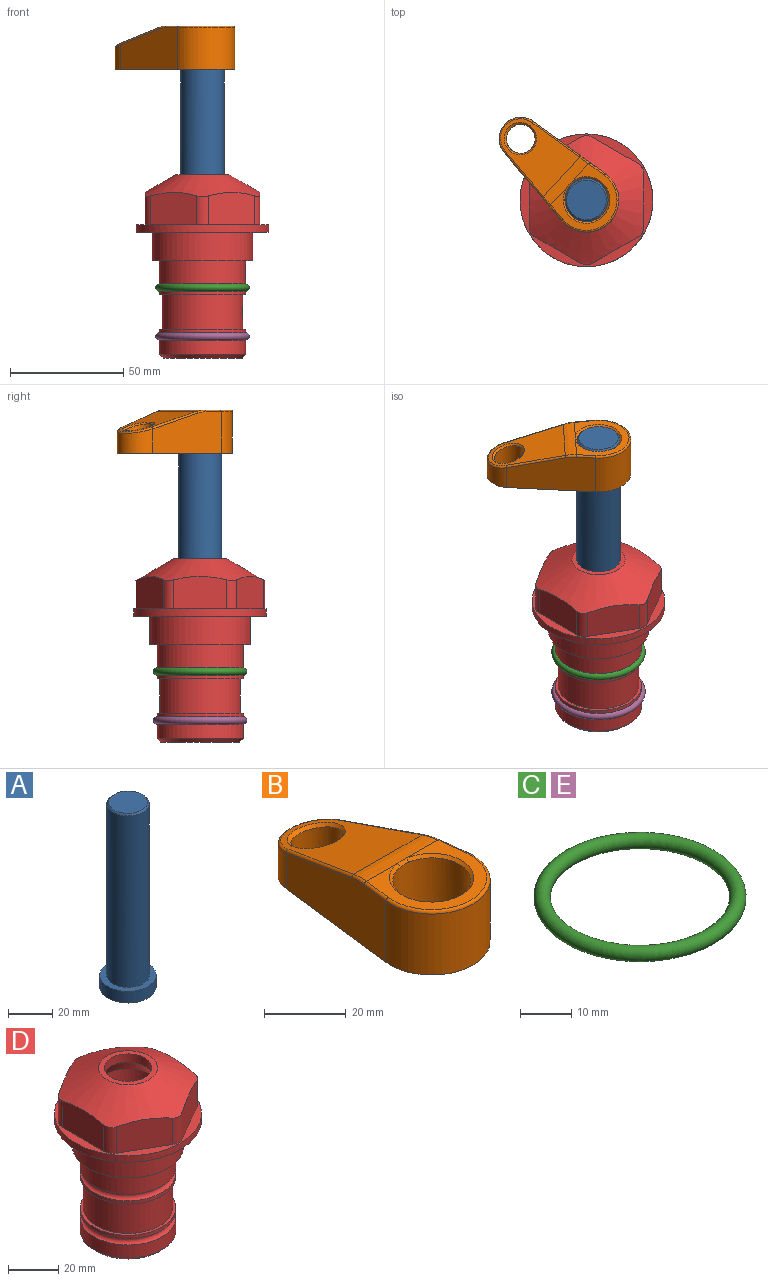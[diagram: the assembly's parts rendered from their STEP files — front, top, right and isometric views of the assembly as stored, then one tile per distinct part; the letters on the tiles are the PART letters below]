
ASSEMBLY  parts=5 mates=4
PART A: 6 faces, bbox 25.4x25.4x101.6 mm
  f0: plane 17.46x17.46mm, normal (0,0,1), area 239.5mm2, adj f5
  f1: plane 25.4x25.4mm, normal (0,0,-1), area 506.7mm2, adj f2
  f2: cylinder r=12.7mm len=25.4mm, axis (0,0,1), area 506.7mm2, adj f1,f3
  f3: plane 25.4x25.4mm, normal (0,0,1), area 221.7mm2, adj f2,f4
  f4: cylinder r=9.53mm len=94.46mm, axis (0,0,1), area 5653mm2, adj f3,f5
  f5: cone r=8.73mm half-angle=45deg, axis (0,0,-1), area 64.4mm2, adj f0,f4
PART B: 31 faces, bbox 31.7x65.5x19.8 mm
  f0: plane 39.12x18.26mm, normal (0.99,0.12,0), area 612.2mm2, adj f1,f4,f7,f11,f13,f15
  f1: cylinder r=9.53mm len=18.91mm, axis (0,0,-1), area 296.1mm2, adj f0,f2,f7,f17
  f2: plane 39.12x18.26mm, normal (-0.99,0.12,0), area 612.2mm2, adj f1,f4,f7,f12,f14,f16
  f3: cylinder r=6.35mm len=12.7mm, axis (0,0,-1), area 362.4mm2, adj f7,f18
  f4: cylinder r=14.29mm len=28.58mm, axis (0,0,-1), area 882.2mm2, adj f0,f2,f7,f10
  f5: cylinder r=9.53mm len=19.05mm, axis (0,0,-1), area 1092.6mm2, adj f7,f19,f20
  f6: plane 26.99x23.69mm, normal (0,0,1), area 216.2mm2, adj f9,f10,f11,f12,f19
  f7: plane 63.5x28.58mm, normal (0,0,-1), area 661.8mm2, adj f0,f1,f2,f3,f4,f5,f22,f23
  f8: plane 33.52x23.6mm, normal (0,0.26,0.97), area 486mm2, adj f9,f15,f16,f17,f18
  f9: cylinder r=19.05mm len=24.72mm, axis (1,0,0), area 120.4mm2, adj f6,f8,f13,f14,f20
  f10: torus R=13.49mm, axis (0,0,1), area 59mm2, adj f4,f6,f11,f12
  f11: cylinder r=0.79mm len=8.67mm, axis (0.12,-0.99,0), area 10.8mm2, adj f0,f6,f10,f13
  f12: cylinder r=0.79mm len=8.67mm, axis (0.12,0.99,0), area 10.8mm2, adj f2,f6,f10,f14
  f13: bspline ~4.95x1.42mm, area 6.1mm2, adj f0,f9,f11,f15
  f14: bspline ~4.95x1.42mm, area 6.1mm2, adj f2,f9,f12,f16
  f15: cylinder r=0.79mm len=25.95mm, axis (0.12,-0.96,0.26), area 32.9mm2, adj f0,f8,f13,f17
  f16: cylinder r=0.79mm len=25.95mm, axis (0.12,0.96,-0.26), area 32.9mm2, adj f2,f8,f14,f17
  f17: bspline ~18.91x8.38mm, area 30mm2, adj f1,f8,f15,f16
  f18: bspline ~14.29x14.29mm, area 48.3mm2, adj f3,f8
  f19: cone r=9.53mm half-angle=45deg, axis (0,0,1), area 66.5mm2, adj f5,f6,f20
  f20: bspline ~3.22x0.96mm, area 3.5mm2, adj f5,f9,f19
  f21: plane 2.75x2.72mm, normal (0,0,-1), area 2.9mm2, adj f23,f25,f28
  f22: plane 23.05x15.88mm, normal (-0.99,-0.12,0), area 323.6mm2, adj f7,f25,f26,f27,f28,f29
  f23: plane 23.05x15.88mm, normal (0.99,-0.12,0), area 323.6mm2, adj f7,f21,f25,f27,f28,f30
  f24: cylinder r=9.53mm len=10.69mm, axis (0,0,-1), area 114.7mm2, adj f7,f27,f29,f30
  f25: cylinder r=12.7mm len=20.59mm, axis (0,0,-1), area 381.1mm2, adj f7,f21,f22,f23,f26,f28
  f26: plane 2.75x2.72mm, normal (0,0,-1), area 2.9mm2, adj f22,f25,f28
  f27: plane 19.72x18.37mm, normal (0,-0.26,-0.97), area 291.8mm2, adj f22,f23,f24,f28,f29,f30
  f28: cylinder r=15.88mm len=19.92mm, axis (1,0,0), area 54.8mm2, adj f21,f22,f23,f25,f26,f27
  f29: cylinder r=1.59mm len=11mm, axis (0,0,-1), area 34.7mm2, adj f7,f22,f24,f27
  f30: cylinder r=1.59mm len=11mm, axis (0,0,-1), area 34.7mm2, adj f7,f23,f24,f27
PART C: 1 faces, bbox 44.7x44.7x3.2 mm
  f0: torus R=19.05mm, axis (0,0,1), area 1193.9mm2
PART D: 36 faces, bbox 58.7x58.7x81 mm
  f0: cylinder r=17.78mm len=35.56mm, axis (0,0,1), area 1670.8mm2, adj f23,f24,f31
  f1: cylinder r=19.05mm len=38.1mm, axis (0,0,1), area 1191.9mm2, adj f26,f27,f30
  f2: plane 58.66x58.66mm, normal (0,0,-1), area 1150.6mm2, adj f3,f28
  f3: cylinder r=29.33mm len=58.66mm, axis (0,0,-1), area 585.1mm2, adj f2,f4
  f4: plane 58.66x58.66mm, normal (0,0,1), area 475.9mm2, adj f3,f5,f6,f7,f8,f9,f10,f11
  f5: plane 20.32x14.34mm, normal (-0.5,0.87,0), area 324.4mm2, adj f4,f15,f16,f17
  f6: plane 20.32x14.34mm, normal (0.5,0.87,0), area 324.4mm2, adj f4,f14,f15,f17
  f7: plane 23.48x14.34mm, normal (1,0,0), area 324.4mm2, adj f4,f13,f14,f17
  f8: plane 20.32x14.34mm, normal (0.5,-0.87,0), area 324.4mm2, adj f4,f12,f13,f17
  f9: plane 20.32x14.34mm, normal (-0.5,-0.87,0), area 324.4mm2, adj f4,f11,f12,f17
  f10: plane 23.48x14.34mm, normal (-1,0,0), area 324.4mm2, adj f4,f11,f16,f17
  f11: cylinder r=5.08mm len=12.85mm, axis (0,0,-1), area 67.2mm2, adj f4,f9,f10,f17
  f12: cylinder r=5.08mm len=12.85mm, axis (0,0,-1), area 67.2mm2, adj f4,f8,f9,f17
  f13: cylinder r=5.08mm len=12.85mm, axis (0,0,-1), area 67.2mm2, adj f4,f7,f8,f17
  f14: cylinder r=5.08mm len=12.85mm, axis (0,0,-1), area 67.2mm2, adj f4,f6,f7,f17
  f15: cylinder r=5.08mm len=12.85mm, axis (0,0,-1), area 67.2mm2, adj f4,f5,f6,f17
  f16: cylinder r=5.08mm len=12.85mm, axis (0,0,-1), area 67.2mm2, adj f4,f5,f10,f17
  f17: cone r=11.73mm half-angle=60deg, axis (0,0,-1), area 2071.8mm2, adj f5,f6,f7,f8,f9,f10,f11,f12
  f18: plane 23.46x23.46mm, normal (0,0,1), area 147.4mm2, adj f17,f35
  f19: plane 34.93x34.93mm, normal (0,0,-1), area 958mm2, adj f29
  f20: cylinder r=19.05mm len=38.1mm, axis (0,0,1), area 760.1mm2, adj f21,f29
  f21: torus R=19.05mm, axis (0,0,1), area 565.3mm2, adj f20,f22
  f22: cylinder r=19.05mm len=38.1mm, axis (0,0,1), area 190mm2, adj f21,f23
  f23: plane 38.1x38.1mm, normal (0,0,1), area 146.9mm2, adj f0,f22
  f24: plane 38.1x38.1mm, normal (0,0,-1), area 146.9mm2, adj f0,f25
  f25: cylinder r=19.05mm len=38.1mm, axis (0,0,1), area 190mm2, adj f24,f26
  f26: torus R=19.05mm, axis (0,0,1), area 565.3mm2, adj f1,f25
  f27: plane 44.45x44.45mm, normal (0,0,-1), area 411.7mm2, adj f1,f28
  f28: cylinder r=22.23mm len=44.45mm, axis (0,0,1), area 1773.5mm2, adj f2,f27
  f29: cone r=19.05mm half-angle=45deg, axis (0,0,1), area 257.5mm2, adj f19,f20
  f30: cylinder r=3.17mm len=6.75mm, axis (-1,0,0), area 128mm2, adj f1,f33
  f31: cylinder r=3.17mm len=6.35mm, axis (-1,0,0), area 102.5mm2, adj f0,f33
  f32: plane 25.4x25.4mm, normal (0,0,1), area 506.7mm2, adj f33
  f33: cylinder r=12.7mm len=66.42mm, axis (0,0,-1), area 5236.2mm2, adj f30,f31,f32,f34
  f34: cone r=9.53mm half-angle=30deg, axis (0,0,-1), area 443.4mm2, adj f33,f35
  f35: cylinder r=9.53mm len=19.05mm, axis (0,0,-1), area 240.9mm2, adj f18,f34
PART E: same geometry as C
PLACE A rot(axis=(0,0,1),47.1deg) t=(0,0,27.55)mm
PLACE B rot(axis=(0,0,1),47.1deg) t=(0,0,27.55)mm
PLACE C at identity
PLACE D at identity fixed
PLACE E t=(0,0,-21.59)mm
MATE fastened E.f0 <-> D.f0  axis (0,0,1) through (0,0,-46.1)mm
MATE cylindrical A.f2 <-> D.f0  axis (0,0,-1) through (0,0,-10.55)mm
MATE fastened A.f2 <-> B.f4  axis (0,0,1) through (0,0,91.05)mm
MATE fastened C.f0 <-> D.f0  axis (0,0,1) through (0,0,-24.51)mm
